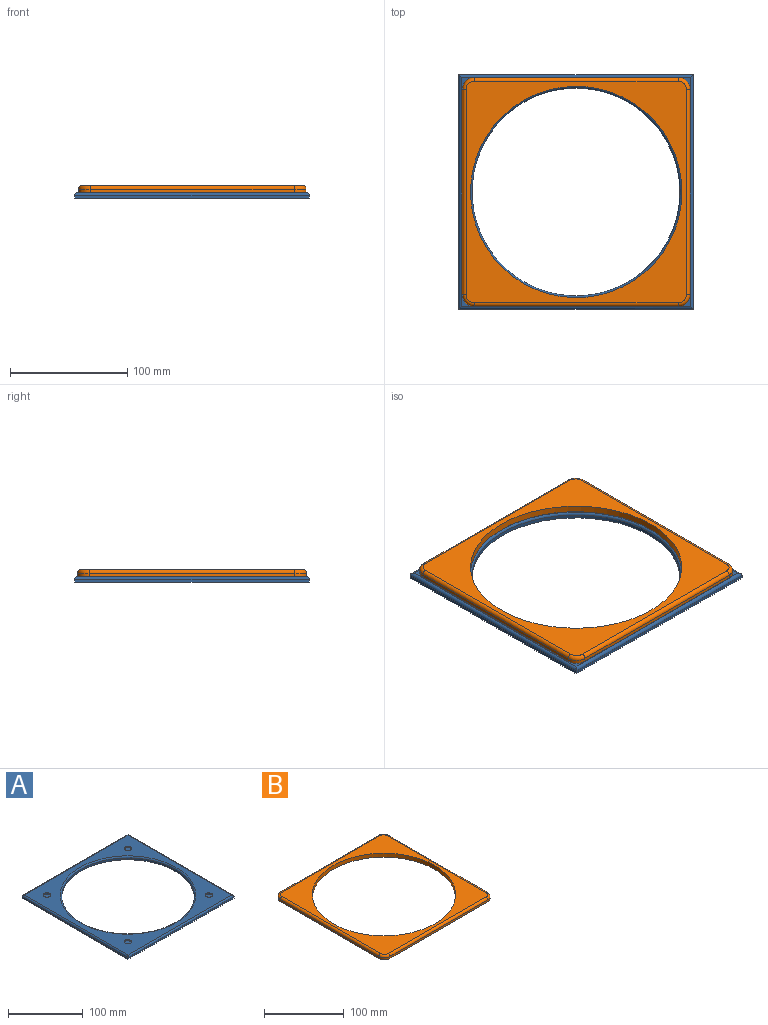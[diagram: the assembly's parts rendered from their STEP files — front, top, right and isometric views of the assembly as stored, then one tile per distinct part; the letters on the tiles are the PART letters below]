
ASSEMBLY  parts=2 mates=1
PART A: 20 faces, bbox 200x200x5 mm
  f0: plane 200x2.5mm, normal (0,1,0), area 500mm2, adj f1,f4,f6,f7
  f1: plane 200x2.5mm, normal (-1,0,0), area 500mm2, adj f0,f2,f6,f8
  f2: plane 200x2.5mm, normal (0,-1,0), area 500mm2, adj f1,f4,f6,f10
  f3: cylinder r=88.5mm len=177mm, axis (0,0,-1), area 1668.2mm2, adj f6,f19
  f4: plane 200x2.5mm, normal (1,0,0), area 500mm2, adj f0,f2,f6,f9
  f5: plane 195x195mm, normal (0,0,1), area 11980.4mm2, adj f7,f8,f9,f10,f11,f13,f15,f17
  f6: plane 200x200mm, normal (0,0,-1), area 15394.3mm2, adj f0,f1,f2,f3,f4
  f7: cylinder r=2.5mm len=200mm, axis (1,0,0), area 778.3mm2, adj f0,f5,f8,f9
  f8: cylinder r=2.5mm len=200mm, axis (0,1,0), area 778.3mm2, adj f1,f5,f7,f10
  f9: cylinder r=2.5mm len=200mm, axis (0,-1,0), area 778.3mm2, adj f4,f5,f7,f10
  f10: cylinder r=2.5mm len=200mm, axis (-1,0,0), area 778.3mm2, adj f2,f5,f8,f9
  f11: cylinder r=5mm len=10mm, axis (0,0,1), area 62.8mm2, adj f5,f12
  f12: plane 10x10mm, normal (0,0,1), area 78.5mm2, adj f11
  f13: cylinder r=5mm len=10mm, axis (0,0,1), area 62.8mm2, adj f5,f14
  f14: plane 10x10mm, normal (0,0,1), area 78.5mm2, adj f13
  f15: cylinder r=5mm len=10mm, axis (0,0,1), area 62.8mm2, adj f5,f16
  f16: plane 10x10mm, normal (0,0,1), area 78.5mm2, adj f15
  f17: cylinder r=5mm len=10mm, axis (0,0,1), area 62.8mm2, adj f5,f18
  f18: plane 10x10mm, normal (0,0,1), area 78.5mm2, adj f17
  f19: torus R=90.5mm, axis (0,0,1), area 1761.3mm2, adj f3,f5
PART B: 27 faces, bbox 195.4x196.6x6 mm
  f0: plane 188.98x187.77mm, normal (0,0,1), area 9995.3mm2, adj f4,f15,f16,f17,f18,f20,f22,f24
  f1: plane 173.77x3mm, normal (0,1,0), area 521.3mm2, adj f6,f15,f23,f25
  f2: plane 174.98x3mm, normal (-1,0,0), area 524.9mm2, adj f6,f16,f21,f23
  f3: plane 173.77x3mm, normal (0,-1,0), area 521.3mm2, adj f6,f18,f19,f21
  f4: cylinder r=90mm len=180mm, axis (0,0,-1), area 3392.9mm2, adj f0,f6
  f5: plane 174.98x3mm, normal (1,0,0), area 524.9mm2, adj f6,f17,f19,f25
  f6: plane 194.98x193.77mm, normal (0,0,-1), area 11933.8mm2, adj f1,f2,f3,f4,f5,f7,f9,f11
  f7: cylinder r=5mm len=10mm, axis (0,0,-1), area 31.4mm2, adj f6,f8
  f8: plane 10x10mm, normal (0,0,-1), area 78.5mm2, adj f7
  f9: cylinder r=5mm len=10mm, axis (0,0,-1), area 31.4mm2, adj f6,f10
  f10: plane 10x10mm, normal (0,0,-1), area 78.5mm2, adj f9
  f11: cylinder r=5mm len=10mm, axis (0,0,-1), area 31.4mm2, adj f6,f12
  f12: plane 10x10mm, normal (0,0,-1), area 78.5mm2, adj f11
  f13: cylinder r=5mm len=10mm, axis (0,0,-1), area 31.4mm2, adj f6,f14
  f14: plane 10x10mm, normal (0,0,-1), area 78.5mm2, adj f13
  f15: cylinder r=3mm len=173.77mm, axis (1,0,0), area 818.9mm2, adj f0,f1,f24,f26
  f16: cylinder r=3mm len=174.98mm, axis (0,1,0), area 824.6mm2, adj f0,f2,f22,f24
  f17: cylinder r=3mm len=174.98mm, axis (0,-1,0), area 824.6mm2, adj f0,f5,f20,f26
  f18: cylinder r=3mm len=173.77mm, axis (-1,0,0), area 818.9mm2, adj f0,f3,f20,f22
  f19: cylinder r=10mm len=10mm, axis (0,0,1), area 47.1mm2, adj f3,f5,f6,f20
  f20: torus R=7mm, axis (0,0,1), area 66mm2, adj f0,f17,f18,f19
  f21: cylinder r=10mm len=10mm, axis (0,0,-1), area 47.1mm2, adj f2,f3,f6,f22
  f22: torus R=7mm, axis (0,0,1), area 66mm2, adj f0,f16,f18,f21
  f23: cylinder r=10mm len=10mm, axis (0,0,1), area 47.1mm2, adj f1,f2,f6,f24
  f24: torus R=7mm, axis (0,0,1), area 66mm2, adj f0,f15,f16,f23
  f25: cylinder r=10mm len=10mm, axis (0,0,-1), area 47.1mm2, adj f1,f5,f6,f26
  f26: torus R=7mm, axis (0,0,1), area 66mm2, adj f0,f15,f17,f25
PLACE A t=(-15.29,-8.7,12.69)mm
PLACE B t=(-15.29,-8.7,-7.31)mm
MATE fastened A.f17 <-> B.f7  axis (0,0,1) through (-91.58,-84.99,17.69)mm
